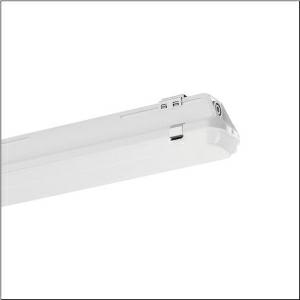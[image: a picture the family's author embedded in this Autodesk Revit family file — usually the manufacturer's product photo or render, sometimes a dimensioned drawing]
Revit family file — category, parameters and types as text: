
# Revit family: monsun_r__12_51fp109p460h_289c
name_source: partatom
category: Lighting Fixtures
units: mm (PartAtom-declared; Revit-internal decimal feet)

## family parameters
Cut with Voids When Loaded = No
Host = Face
Light Source = No
Part Type = Normal
Room Calculation Point = No
Round Connector Dimension = Use Diameter
Shared = No

## types (1)
- Monsun® 12 (1 x LED, 6100 lm, 34 W, 4000K)
    Apparent Load = 34 VA
    CIE Flux Codes = 47 77 93 94 100
    Color Rendering = 80
    Color Temperature = 4000K
    Default Elevation = 1800 mm
    Description = Monsun® 12, damp-proof luminaire, chain hanger, primary optical cover: enclosure, of PMMA, light emission: direct distribution, primary light characteristic: symmetric, installation type: suspended mounting, surface-mounted, horizontal mounting, vertical mounting, LED, rated luminous flux: 6.100lm, luminous efficacy: 179lm/W, light colour: 840, colour temperature: 4000K, control gear: ECG, with terminal, 3-pole, max. 2.5mm², mains connection: 220..240V, AC, 50/60Hz, start of lifetime: 34W, end of lifetime: 38W, luminaire housing, of glass-fibre reinforced polyester, uncoated, bright grey, length: 1.590mm, width: 90mm, height: 88mm, clip for enclosure, of stainless steel (V2A), ceiling mounting element, of stainless steel (V2A), chain hanger, of stainless steel (V2A), protection rating (complete): IP66, insulation class (complete): insulation class I (protective earthing), certification: CE, ENEC, VDE, protection symbol: D, impact resistance: IK04, permissible operating ambient temperature: -35..+40°C, standard: EN 50419, EN 60598-2-1, no direct snow, no direct sun, no direct rain, for indoor or canopied outdoor use, corresponds to IFS (International Featured Standards) requirements for safety and quality in the food industry, for animal farming (ammonia tested): for use in cowhouse, pig house, horse-stables... (not for use in poultry stables), AT max for animal farming = 40°C, packaging unit: 1 piece
    Height = 89 mm
    Lamp = 1 x LED
    Lamp Light Flux = 6100 lm
    Lamp Power = 34 W
    Lamp count = 1
    Length = 1590 mm
    Luminous efficacy = 179 lm/W
    Manufacturer = Siteco
    ModVariant = No
    Model = 51FP109P460H
    Mounting Place = Ceiling
    Mounting Type = Pendant
    Number of Poles = 1
    OnlyDefault = Yes
    Power Factor = 1
    Product Name = Monsun® 12
    Product group = damp-proof luminaire | ceiling pendant
    ProductGroupID = 908
    Protection Class = Protection class I
    Protection Degree = IP 66
    RLX_Detail_Level = 1
    RlxData = <blob elided: 88477 chars, md5=eccd0f8e>
    Socket = socket
    Standby Power = 0 W
    System Light Flux = 6100 lm
    System Power = 34 W
    Type Comments = Product without accessories
    Type Image = l_1004748.jpg
    URL = http://relux.com
    VarID = ---
    Voltage = 0 V
    Weight = 0.00 kg
    Width = 90 mm

## geometry (parser evidence)
native form markers: Blend x4, Sweep x13
no freeform markers — native parametric forms only
